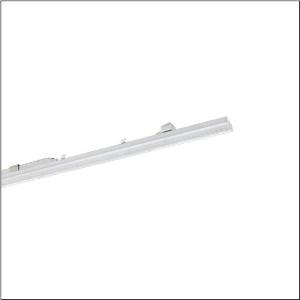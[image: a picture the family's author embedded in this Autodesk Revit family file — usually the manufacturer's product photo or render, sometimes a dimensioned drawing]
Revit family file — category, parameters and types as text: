
# Revit family: tl_l_5wd7a8p0g2b5
name_source: partatom
category: Lighting Fixtures
units: mm (PartAtom-declared; Revit-internal decimal feet)

## family parameters
Cut with Voids When Loaded = No
Host = Face
Light Source = No
Part Type = Normal
Room Calculation Point = No
Round Connector Dimension = Use Diameter
Shared = No

## types (1)
- --- (1 x LED, 5000 lm, 31.5 W, 4000K)
    Apparent Load = 32 VA
    CIE Flux Codes = 49 84 98 100 100
    Color Rendering = 80
    Color Temperature = 4000K
    Default Elevation = 1800 mm
    Description = TL L, luminaire insert, of sheet steel, galvanised, coil coated, white, length: 1.500mm, width: 66mm, height: 67mm, surge protection,LED light colour: 840, control gear: DALI, with terminal, 5-pole, mains connection: 230..240V, AC, 50/60Hz, rated input power: 63W, primary optical cover: cover, of PMMA, light emission: direct distribution, protection rating (complete): as luminaire, insulation class (complete): insulation class I (protective earthing), certification: CE, impact resistance: IK06, permissible ambient temperature for indoor applications: -35..+35°C, standard: NMF01, packaging unit: 1 piece
    Height = 120 mm
    Lamp = 1 x LED
    Lamp Light Flux = 5000 lm
    Lamp Power = 31.5 W
    Lamp count = 1
    Length = 1690 mm
    Luminous efficacy = 159 lm/W
    Manufacturer = Siteco
    ModVariant = No
    Model = 5WD7A8P0G2B5
    Mounting Place = Ceiling
    Mounting Type = Pendant
    Number of Poles = 1
    OnlyDefault = Yes
    Power Factor = 1
    Product Name = TL L
    Product group = luminaire insert
    ProductGroupID = 901
    Protection Class = Protection class I
    Protection Degree = Degree of protection
    RLX_Detail_Level = 1
    RLX_Emergency_Light_Flux = 0 lm
    RLX_Emergency_Type = 0
    RLX_Emergency_Type_DB = No
    RlxData = <blob elided: 17361 chars, md5=e56e489c>
    Socket = socket
    Standby Power = 0 W
    System Light Flux = 5000 lm
    System Power = 32 W
    Type Comments = factory setting: luminous flux: 100 % | dim-lin: 254 | 646 mA
    Type Image = l_1294382.jpg
    URL = http://relux.com
    VarID = @adj_016697
    Voltage = 0 V
    Weight = 0.00 kg
    Width = 208 mm

## geometry (parser evidence)
native form markers: Blend x4, Sweep x11
no freeform markers — native parametric forms only
